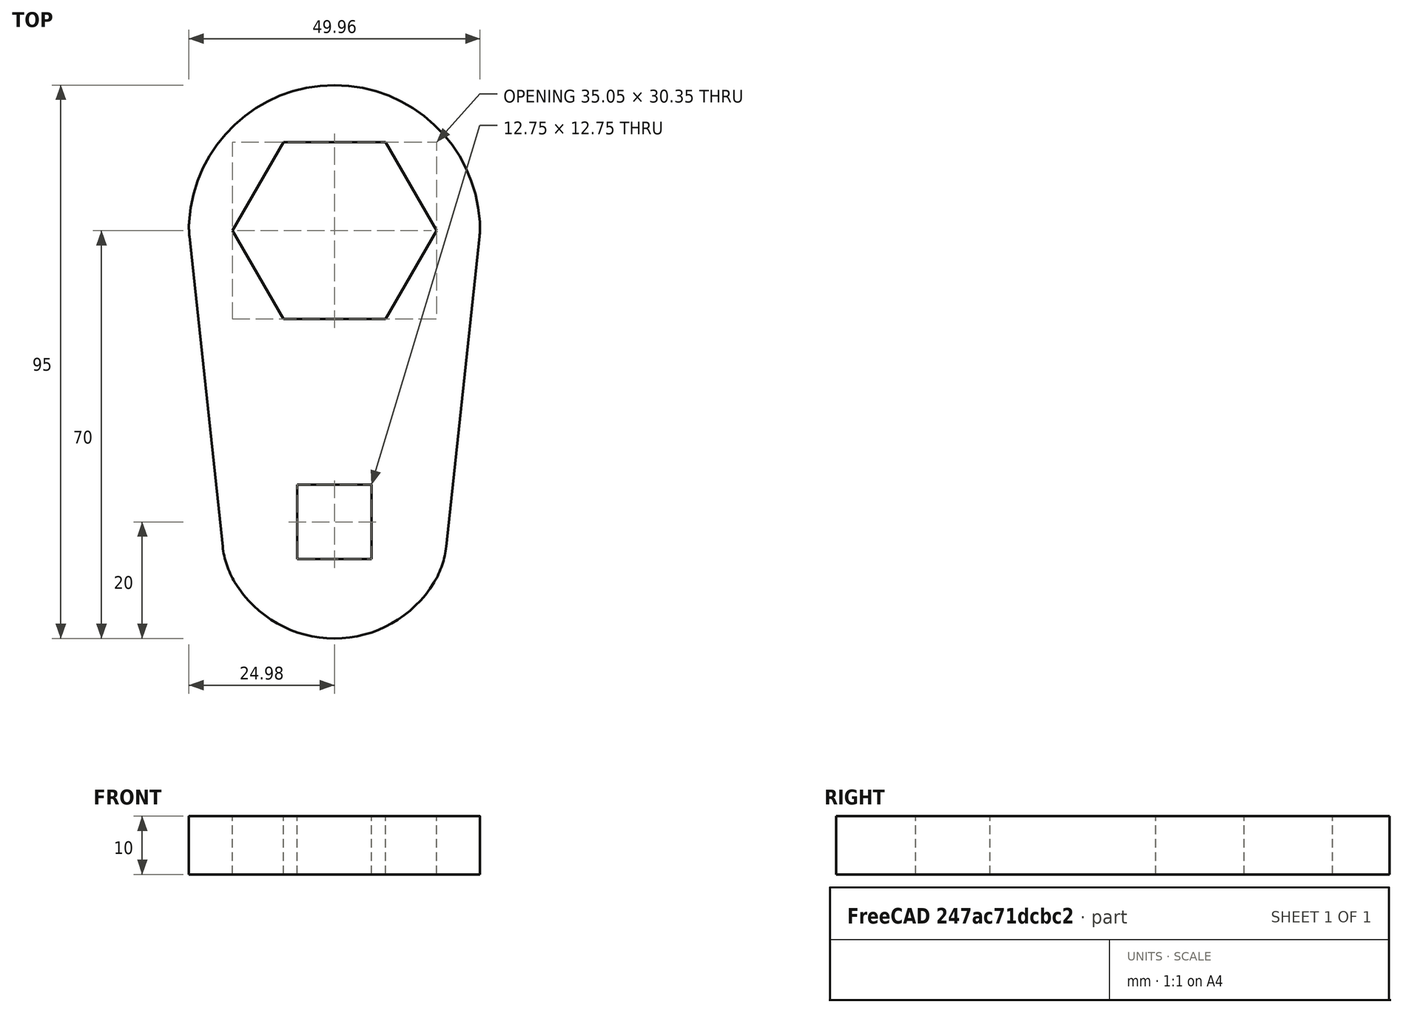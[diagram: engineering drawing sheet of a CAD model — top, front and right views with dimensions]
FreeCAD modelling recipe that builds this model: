
FCSTD DOCUMENT  (FreeCAD 0.18R16131 (Git))
Label: transmission wrench 35 13 w fea
License: All rights reserved
LicenseURL: http://en.wikipedia.org/wiki/All_rights_reserved
objects: Fem::FemMeshObjectPython×2, Sketcher::SketchObject×1, PartDesign::Pad×1, PartDesign::Fillet×1, PartDesign::Body×1, Fem::FemSolverObjectPython×1, App::MaterialObjectPython×1, Fem::ConstraintFixed×1, Fem::ConstraintForce×1, Fem::FemResultObjectPython×1, Fem::FemAnalysis×1
note: 5 computed .brp shape members not serialized (recipe doc carries the construction recipe); baked Part::Feature solids carry a one-line shape summary decoded from their .brp

FEATURE [Sketcher::SketchObject] Sketch
  MapMode = 5
  Support = -> [XY_Plane]
  expr: Constraints[29] = 25.4 * 0.5 + 0.05
  sketch-geometry (17):
    g0: LineSegment StartX=-17.525 StartY=0 StartZ=0 EndX=-8.7625 EndY=-15.1771 EndZ=0
    g1: LineSegment StartX=-8.7625 StartY=-15.1771 StartZ=0 EndX=8.7625 EndY=-15.1771 EndZ=0
    g2: LineSegment StartX=8.7625 StartY=-15.1771 StartZ=0 EndX=17.525 EndY=0 EndZ=0
    g3: LineSegment StartX=17.525 StartY=0 StartZ=0 EndX=8.7625 EndY=15.1771 EndZ=0
    g4: LineSegment StartX=8.7625 StartY=15.1771 StartZ=0 EndX=-8.7625 EndY=15.1771 EndZ=0
    g5: LineSegment StartX=-8.7625 StartY=15.1771 StartZ=0 EndX=-17.525 EndY=0 EndZ=0
    g6: Circle [constr] CenterX=0 CenterY=0 CenterZ=0 NormalX=0 NormalY=0 NormalZ=1 AngleXU=0 Radius=17.525
    g7: LineSegment StartX=6.375 StartY=-56.375 StartZ=0 EndX=6.375 EndY=-43.625 EndZ=0
    g8: LineSegment StartX=6.375 StartY=-43.625 StartZ=0 EndX=-6.375 EndY=-43.625 EndZ=0
    g9: LineSegment StartX=-6.375 StartY=-43.625 StartZ=0 EndX=-6.375 EndY=-56.375 EndZ=0
    g10: LineSegment StartX=-6.375 StartY=-56.375 StartZ=0 EndX=6.375 EndY=-56.375 EndZ=0
    g11: Circle [constr] CenterX=0 CenterY=-50 CenterZ=0 NormalX=0 NormalY=0 NormalZ=1 AngleXU=0 Radius=9.01561
    g12: ArcOfCircle CenterX=0 CenterY=0 CenterZ=0 NormalX=0 NormalY=0 NormalZ=1 AngleXU=0 Radius=25 StartAngle=0 EndAngle=3.14159
    g13: ArcOfCircle CenterX=0 CenterY=-50 CenterZ=0 NormalX=0 NormalY=0 NormalZ=1 AngleXU=0 Radius=20 StartAngle=3.466 EndAngle=5.95877
    g14: LineSegment StartX=-25 StartY=0 StartZ=0 EndX=-18.9568 EndY=-56.375 EndZ=0
    g15: LineSegment StartX=18.9568 StartY=-56.375 StartZ=0 EndX=25 EndY=0 EndZ=0
    g16: LineSegment [constr] StartX=-18.9568 StartY=-56.375 StartZ=0 EndX=18.9568 EndY=-56.375 EndZ=0
  constraints (44):
    c: Coincident(g0,g1)
    c: Coincident(g1,g2)
    c: Coincident(g2,g3)
    c: Coincident(g3,g4)
    c: Coincident(g4,g5)
    c: Coincident(g5,g0)
    c: Equal(g0, g1-g5) x5
    c: PointOnObject(g0,g6)
    c: PointOnObject(g1,g6)
    c: PointOnObject(g2,g6)
    c: PointOnObject(g3,g6)
    c: Symmetric(g0,g2,g-1)
    c: Coincident(g7,g8)
    c: Coincident(g8,g9)
    c: Coincident(g9,g10)
    c: Coincident(g10,g7)
    c: Equal(g7,g8)
    c: Equal(g7,g9)
    c: Equal(g7,g10)
    c: PointOnObject(g7,g11)
    c: PointOnObject(g8,g11)
    c: PointOnObject(g9,g11)
    c: PointOnObject(g10,g11)
    c: PointOnObject(g11,g-2)
    c: Parallel(g8,g-1)
    c: DistanceX(g9,g7) = 12.75
    c: DistanceY(g11,g-1) = 50
    c: PointOnObject(g12,g-1)
    c: PointOnObject(g12,g-1)
    c: Coincident(g14,g12)
    c: Coincident(g15,g12)
    c: Coincident(g12,g-1)
    c: Radius(g12) = 25
    c: Radius(g13) = 20
    c: Coincident(g15,g13)
    c: Coincident(g13,g14)
    c: Coincident(g13,g11)
    c: Coincident(g13,g16)
    c: Coincident(g16,g13)
    c: Parallel(g16,g-1)
    c: PointOnObject(g7,g16)
    c: Coincident(g6,g12)
    c: PointOnObject(g0,g-1)
    c: DistanceX(g0,g2) = 35.05
FEATURE [PartDesign::Pad] Pad
  Length = 10
  Length2 = 100
  Profile = -> Sketch
  Type = 0
FEATURE [PartDesign::Fillet] Fillet
  Base = -> Pad [Edge2,Edge5,Edge8,Edge1]
  BaseFeature = -> Pad
  Radius = 15
FEATURE [PartDesign::Body] Body
  Group = -> [Sketch,Pad,Fillet]
  Origin = -> Origin
  Tip = -> Fillet
FEATURE [Fem::FemSolverObjectPython] CalculiXccxTools  # FEM object (typed FeaturePython)
  AnalysisType = 0
  BeamShellResultOutput3D = false
  EigenmodeHighLimit = 1000000
  EigenmodeLowLimit = 0
  EigenmodesCount = 10
  GeometricalNonlinearity = 0
  IterationsControlParameterCutb = 0.25,0.5,0.75,0.85,,,1.5,
  IterationsControlParameterIter = 4,8,9,200,10,400,,200,,
  IterationsControlParameterTimeUse = false
  IterationsThermoMechMaximum = 200
  IterationsUserDefinedIncrementations = false
  IterationsUserDefinedTimeStepLength = false
  MaterialNonlinearity = 0
  MatrixSolverType = 0
  SplitInputWriter = false
  ThermoMechSteadyState = true
  TimeEnd = 1
  TimeInitialStep = 1
FEATURE [Fem::FemMeshObjectPython] FEMMeshGmsh  # FEM object (typed FeaturePython)
  Algorithm2D = 0
  Algorithm3D = 0
  CharacteristicLengthMax = 0
  CharacteristicLengthMin = 0
  CoherenceMesh = true
  ElementDimension = 0
  ElementOrder = 1
  GeometryTolerance = 1e-06
  GroupsOfNodes = false
  HighOrderOptimize = false
  OptimizeNetgen = false
  OptimizeStd = true
  Part = -> Fillet
  RecombineAll = false
FEATURE [App::MaterialObjectPython] SolidMaterial  # material (typed FeaturePython)
  Category = 0
  Material = Density=7900 kg/m^3,Description=Standard steel material for CalculiX sample calculations,Father=Metal,Name=CalculiX-Steel,PoissonRatio=0.3,+4 more (map truncated)
FEATURE [Fem::ConstraintFixed] FemConstraintFixed
  NormalDirection = (0.866025,0.5,0)
  Normals = (54) [(0.866025,0.5,0),(0.866025,0.5,0),(0.866025,0.5,0),(0.866025,0.5,0),(0.866025,0.5,0),(0.866025,0.5,0),(0.866025,0.5,0),(0.866025,0.5,0),+46 more]
  Points = (54) [(-17.525,0,10),(-13.1437,-7.58855,10),(-8.7625,-15.1771,10),(-17.525,0,5),(-13.1437,-7.58855,5),(-8.7625,-15.1771,5),(-17.525,0,0),+47 more]
  References = -> [Fillet]
FEATURE [Fem::ConstraintForce] FemConstraintForce
  DirectionVector = (-1,-1e-16,0)
  Force = 8300
  NormalDirection = (1,1e-16,0)
  Points = (9) [(-6.375,-43.625,10),(-6.375,-50,10),(-6.375,-56.375,10),(-6.375,-43.625,5),(-6.375,-50,5),(-6.375,-56.375,5),(-6.375,-43.625,0),(-6.375,-50,0),+1 more]
  References = -> [Fillet]
  Reversed = true
FEATURE [Fem::FemMeshObjectPython] Result_mesh  # FEM object (typed FeaturePython)
FEATURE [Fem::FemResultObjectPython] CalculiX_static_results  # FEM object (typed FeaturePython)
  DisplacementLengths = [0.00118171,0.00126304,0.0012003,0.00127216,0.00140718,0.00152727,0.0290341,0.0333211,0.0336924,0.0359276,0,0,0,0,0,0,0.0335925,0.0302632,0.0197198,0.016816,0.00144109,0.00151847,0.0290323,0.0333763,0.0336861,0.0359744,0,0,0,0,0,0,0.0337283,+1162 more]
  DisplacementVectors = (1195) [(-7.35734e-05,-0.00117221,0.000130188),(-7.15032e-05,0.00125307,-0.000141288),(-7.88314e-05,-0.00119043,-0.000131861),+1192 more]
  Eigenmode = 0
  EigenmodeFrequency = 0
  MaxShear = [10.3638,10.3173,9.82901,10.8242,10.2439,11.0189,4.67343,21.8698,6.67458,19.2159,2.53987,19.5589,2.43526,18.6809,40.8884,38.5553,24.3771,33.9749,63.5907,26.6842,10.2149,11.1126,4.51529,21.9902,6.82175,19.1274,2.36192,19.6745,2.23223,19.7608,+1165 more]
  Mesh = -> Result_mesh
  NodeNumbers = [1,2,3,4,5,6,7,8,9,10,11,12,13,14,15,16,17,18,19,20,21,22,23,24,25,26,27,28,29,30,31,32,33,34,35,36,37,38,39,40,41,42,43,44,45,46,47,48,49,50,51,52,53,54,55,56,57,58,59,60,61,62,63,64,65,66,67,68,69,+1126 more]
  PrincipalMax = [19.9631,-0.0533591,19.3642,1.5426,18.5345,1.63776,7.80365,43.9993,0.27962,38.5356,1.90788,16.5021,3.02763,20.3949,62.1179,17.4027,3.3327,77.2985,142.413,-10.8434,18.8111,1.99706,7.55662,44.2559,0.212739,38.1539,1.93851,16.4606,2.64301,+1166 more]
  PrincipalMed = [0.680182,-0.664419,0.275817,0.0831908,-0.0848354,0.0730263,-0.478094,2.37617,-0.0580131,0.436782,-0.270437,-0.518303,0.256271,0.264151,11.7857,-10.429,-2.84105,16.2813,24.1048,-14.5062,-0.448503,0.422751,-0.394126,2.35983,0.0222148,0.29669,+1169 more]
  PrincipalMin = [-0.764565,-20.6879,-0.293826,-20.1057,-1.95343,-20.4,-1.54321,0.259743,-13.0695,0.103845,-3.17187,-22.6157,-1.8429,-16.967,-19.6589,-59.7079,-45.4215,9.3486,15.2312,-64.2119,-1.61861,-20.2282,-1.47397,0.275442,-13.4308,-0.100868,-2.78534,+1168 more]
  ResultType = Fem::FemResultMechanical
  Stats = [-0.0375914,-0.0132685,0.000181493,-0.0108073,0.00019241,0.0121669,-0.000810547,1.40627e-05,0.000960866,0,0.0140452,0.0375927,0.097767,34.6643,146.834,-23.4744,20.2233,181.558,-81.4528,-0.623776,36.7655,-99.8027,-17.3644,32.7636,0.0560981,+14 more]
  StrainVectors = (1195) [(-3.00753e-05,9.20913e-05,-2.41518e-05),(2.84947e-05,-9.60913e-05,2.68238e-05),(-2.79976e-05,9.1385e-05,-2.65375e-05),+1192 more]
  StressValues = [20.0444,20.3359,19.3795,20.9568,19.6204,21.2986,8.86244,42.7207,13.1836,38.2664,4.41402,33.9719,4.23137,32.3888,71.4477,67.6353,45.9793,64.7624,122.985,51.6346,19.8706,21.4814,8.54201,42.9762,13.5492,38.0576,4.10051,34.1613,3.87604,34.4139,+1165 more]
  StressVectors = (1195) [(-0.270932,19.4637,0.685941),(-0.336776,-20.4622,-0.606691),(-0.0581799,19.2267,0.177672),(1.19248,-19.7617,0.0892719),(-0.0448309,18.2611,-1.72007),+1190 more]
  Time = 0
FEATURE [Fem::FemAnalysis] Analysis
  Group = -> [CalculiXccxTools,FEMMeshGmsh,SolidMaterial,FemConstraintFixed,FemConstraintForce,CalculiX_static_results]
